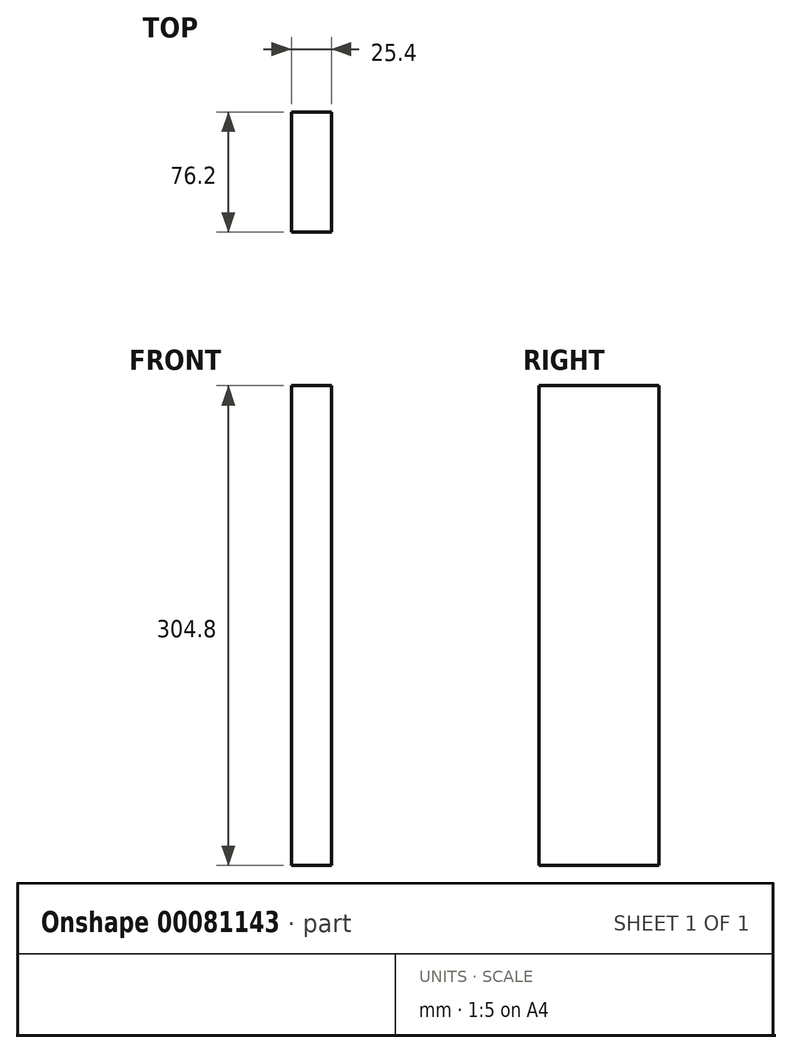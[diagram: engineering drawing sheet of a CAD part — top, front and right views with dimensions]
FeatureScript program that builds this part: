
annotation { "Feature Type Name" : "Feature", "Feature Type Description" : "" }
export const myFeature = defineFeature(function(context is Context, id is Id, definition is map)
    precondition{}
    {
        {
            var Q0;
            Q0=qCreatedBy(makeId("Top.planeOp"),FACE);
            var sketch = newSketch(context, id + "F0", { "sketchPlane" : qUnion([Q0])});
            skLineSegment(sketch, "E0.bottom", {"start": v(-12.7, 38.1) * mm, "end": v(12.7, 38.1) * mm});
            skLineSegment(sketch, "E0.top", {"start": v(-12.7, -38.1) * mm, "end": v(12.7, -38.1) * mm});
            skLineSegment(sketch, "E0.left", {"start": v(-12.7, 38.1) * mm, "end": v(-12.7, -38.1) * mm});
            skLineSegment(sketch, "E0.right", {"start": v(12.7, 38.1) * mm, "end": v(12.7, -38.1) * mm});
            skPoint(sketch, "E0.middle", {"position": v(0, 0) * mm});
            skSolve(sketch);
        }
        {
            var Q0;
            Q0=makeQuery(id+"F0.imprint","IMPRINT",FACE,{"disambiguationData":[TD([[makeQuery(id+"F0.imprint","IMPRINT",EDGE,{"derivedFrom":sQuery(id+"F0.wireOp",EDGE,"E0.bottom")}),-1.0]])]});
            extrude(context, id + "F1", {"entities" : qUnion([Q0]), "depth" : 304.8 * mm});
        }
    });
